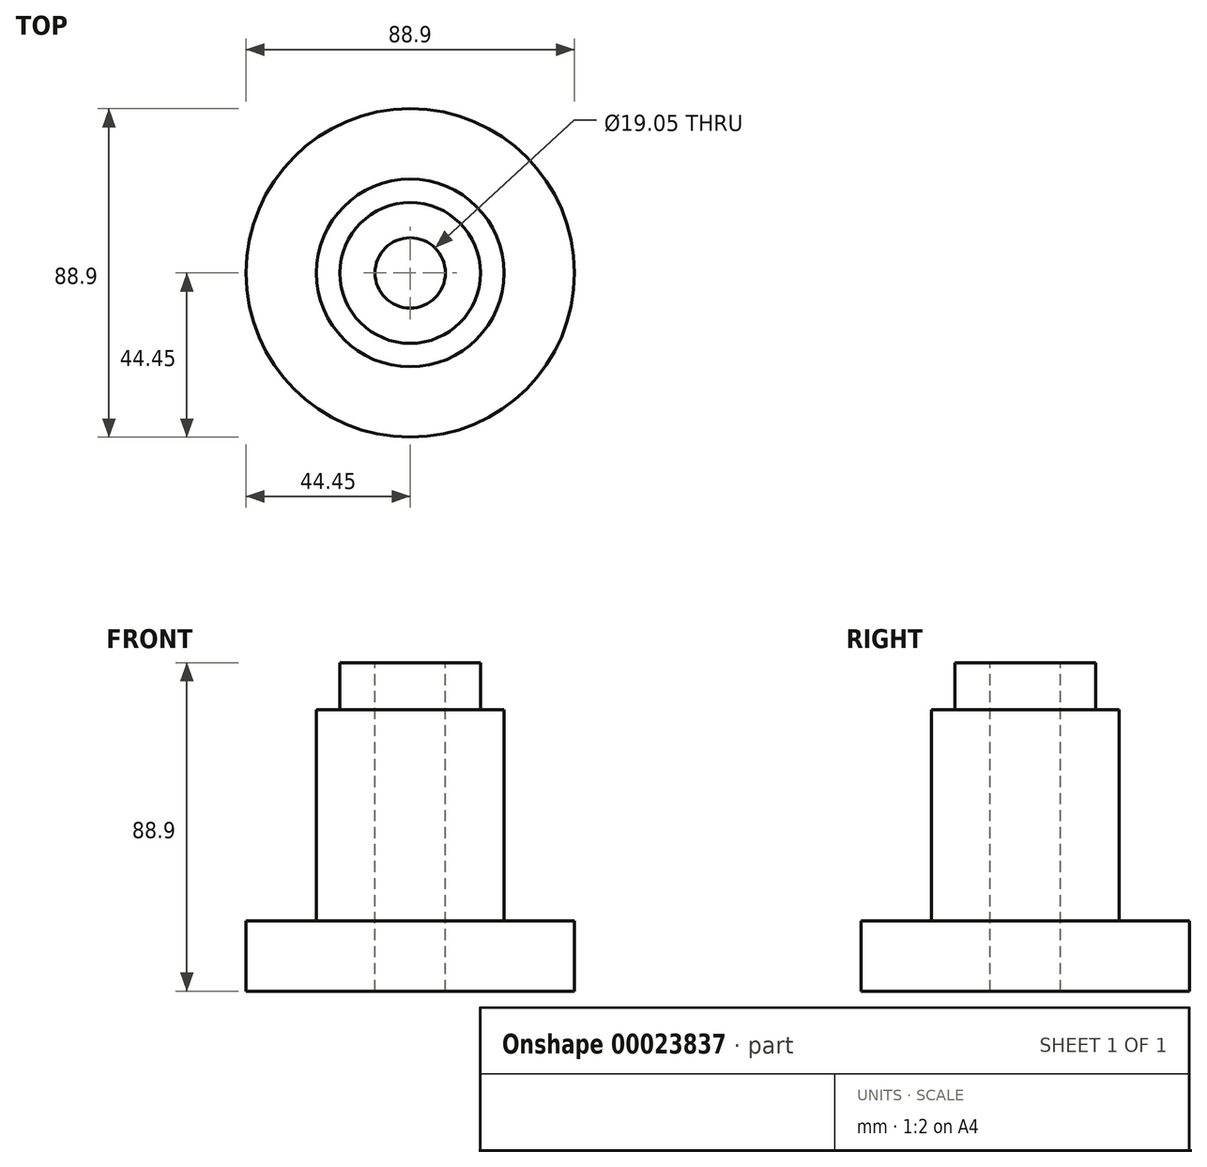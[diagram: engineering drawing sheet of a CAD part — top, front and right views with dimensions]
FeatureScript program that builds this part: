
annotation { "Feature Type Name" : "Feature", "Feature Type Description" : "" }
export const myFeature = defineFeature(function(context is Context, id is Id, definition is map)
    precondition{}
    {
        {
            var Q0;
            Q0=qCreatedBy(makeId("Front.planeOp"),FACE);
            var sketch = newSketch(context, id + "F0", { "sketchPlane" : qUnion([Q0])});
            skLineSegment(sketch, "E0", {"start": v(0, 64.63) * mm, "end": v(0, -47.25) * mm, "construction": true});
            skLineSegment(sketch, "E1.bottom", {"start": v(-9.52, -34.02) * mm, "end": v(-44.45, -34.02) * mm});
            skLineSegment(sketch, "E1.top", {"start": v(-9.52, -14.97) * mm, "end": v(-44.45, -14.97) * mm});
            skLineSegment(sketch, "E1.left", {"start": v(-9.52, -34.02) * mm, "end": v(-9.52, -14.97) * mm});
            skLineSegment(sketch, "E1.right", {"start": v(-44.45, -34.02) * mm, "end": v(-44.45, -14.97) * mm});
            skLineSegment(sketch, "E2.bottom", {"start": v(-9.52, -14.97) * mm, "end": v(-25.4, -14.97) * mm});
            skLineSegment(sketch, "E2.top", {"start": v(-9.53, 42.18) * mm, "end": v(-25.4, 42.18) * mm});
            skLineSegment(sketch, "E2.left", {"start": v(-9.52, -14.97) * mm, "end": v(-9.53, 42.18) * mm});
            skLineSegment(sketch, "E2.right", {"start": v(-25.4, -14.97) * mm, "end": v(-25.4, 42.18) * mm});
            skLineSegment(sketch, "E3.bottom", {"start": v(-9.53, 42.18) * mm, "end": v(-19.05, 42.18) * mm});
            skLineSegment(sketch, "E3.top", {"start": v(-9.53, 54.88) * mm, "end": v(-19.05, 54.88) * mm});
            skLineSegment(sketch, "E3.left", {"start": v(-9.53, 42.18) * mm, "end": v(-9.53, 54.88) * mm});
            skLineSegment(sketch, "E3.right", {"start": v(-19.05, 42.18) * mm, "end": v(-19.05, 54.88) * mm});
            skSolve(sketch);
        }
        {
            var Q0;
            Q0 = qSketchRegion(id + "F0", true);
            var Q1;
            Q1=sQuery(id+"F0.wireOp",EDGE,"E0");
            revolve(context, id + "F1", {"entities" : qUnion([Q0]), "axis" : qUnion([Q1]), "revolveType" : RevolveType.FULL});
        }
    });
